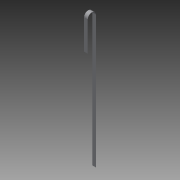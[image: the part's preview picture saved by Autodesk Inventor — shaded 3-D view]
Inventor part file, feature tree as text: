
AUTODESK INVENTOR PART (.ipt)
format: ipt  version: 2013 (Build 170138000, 138)  size: 93,696 bytes
history: native  units: in
note: dims shown in document units (in); Inventor stores cm internally (conversion verified against a paired STEP export)
features: extrude x1
ambient origin geometry x8: Origin, YZ Plane, XZ Plane, XY Plane, X Axis, Y Axis, Z Axis, Center Point
feature tree (1):
  extrude  "Extrusion2"  Depth=1.1in
